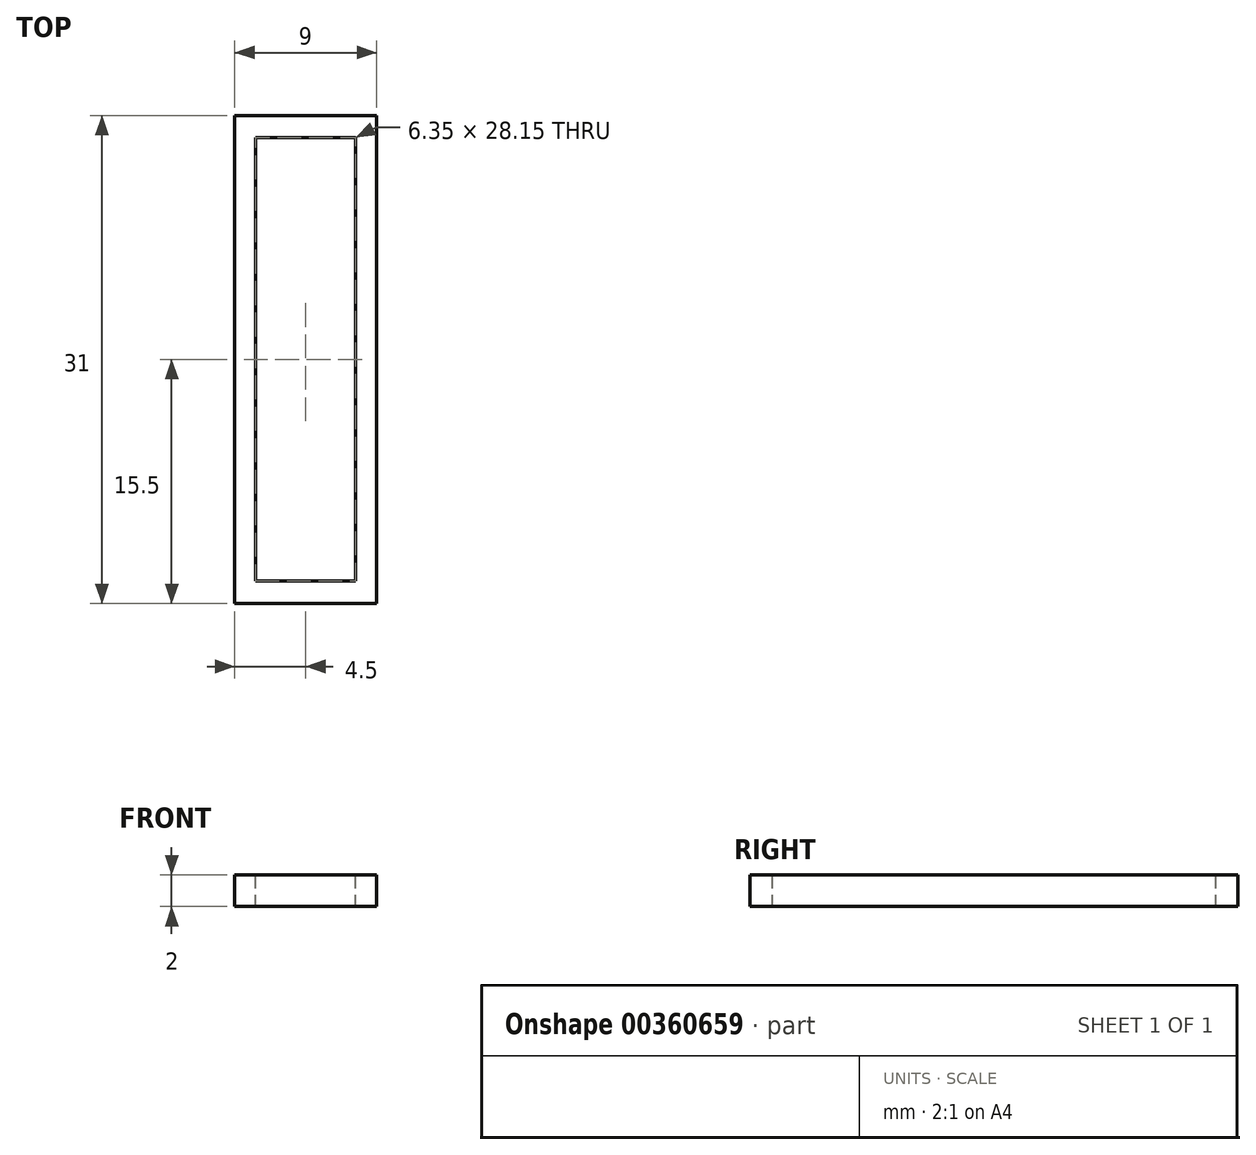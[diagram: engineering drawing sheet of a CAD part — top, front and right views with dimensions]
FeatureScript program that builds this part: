
annotation { "Feature Type Name" : "Feature", "Feature Type Description" : "" }
export const myFeature = defineFeature(function(context is Context, id is Id, definition is map)
    precondition{}
    {
        {
            var Q0;
            Q0=qCreatedBy(makeId("Top.planeOp"),FACE);
            var sketch = newSketch(context, id + "F0", { "sketchPlane" : qUnion([Q0])});
            skLineSegment(sketch, "E0.bottom", {"start": v(4.5, 15.5) * mm, "end": v(-4.5, 15.5) * mm});
            skLineSegment(sketch, "E0.top", {"start": v(4.5, -15.5) * mm, "end": v(-4.5, -15.5) * mm});
            skLineSegment(sketch, "E0.left", {"start": v(4.5, 15.5) * mm, "end": v(4.5, -15.5) * mm});
            skLineSegment(sketch, "E0.right", {"start": v(-4.5, 15.5) * mm, "end": v(-4.5, -15.5) * mm});
            skPoint(sketch, "E0.middle", {"position": v(0, 0) * mm});
            skSolve(sketch);
        }
        {
            var Q0;
            Q0 = qSketchRegion(id + "F0", true);
            extrude(context, id + "F1", {"entities" : qUnion([Q0]), "depth" : 2 * mm});
        }
        {
            var Q0;
            Q0=qCreatedBy(makeId("Top.planeOp"),FACE);
            cPlane(context, id + "F2", {"entities" : qUnion([Q0]), "cplaneType" : CPlaneType.OFFSET, "offset" : 2 * mm, "width" : 150 * mm, "height" : 150 * mm});
        }
        {
            var Q0;
            Q0=qCreatedBy(id+"F2.planeOp",FACE);
            var sketch = newSketch(context, id + "F3", { "sketchPlane" : qUnion([Q0])});
            skLineSegment(sketch, "E1.bottom", {"start": v(3.17, -14.07) * mm, "end": v(-3.18, -14.07) * mm});
            skLineSegment(sketch, "E1.top", {"start": v(3.17, 14.07) * mm, "end": v(-3.18, 14.07) * mm});
            skLineSegment(sketch, "E1.left", {"start": v(3.18, -14.07) * mm, "end": v(3.18, 14.07) * mm});
            skLineSegment(sketch, "E1.right", {"start": v(-3.17, -14.07) * mm, "end": v(-3.17, 14.07) * mm});
            skPoint(sketch, "E1.middle", {"position": v(0, 0) * mm});
            skSolve(sketch);
        }
        {
            var Q0;
            Q0 = qSketchRegion(id + "F3", true);
            extrude(context, id + "F4", {"entities" : qUnion([Q0]), "operationType" : NewBodyOperationType.REMOVE, "oppositeDirection" : true, "depth" : 15.9 * mm});
        }
    });
